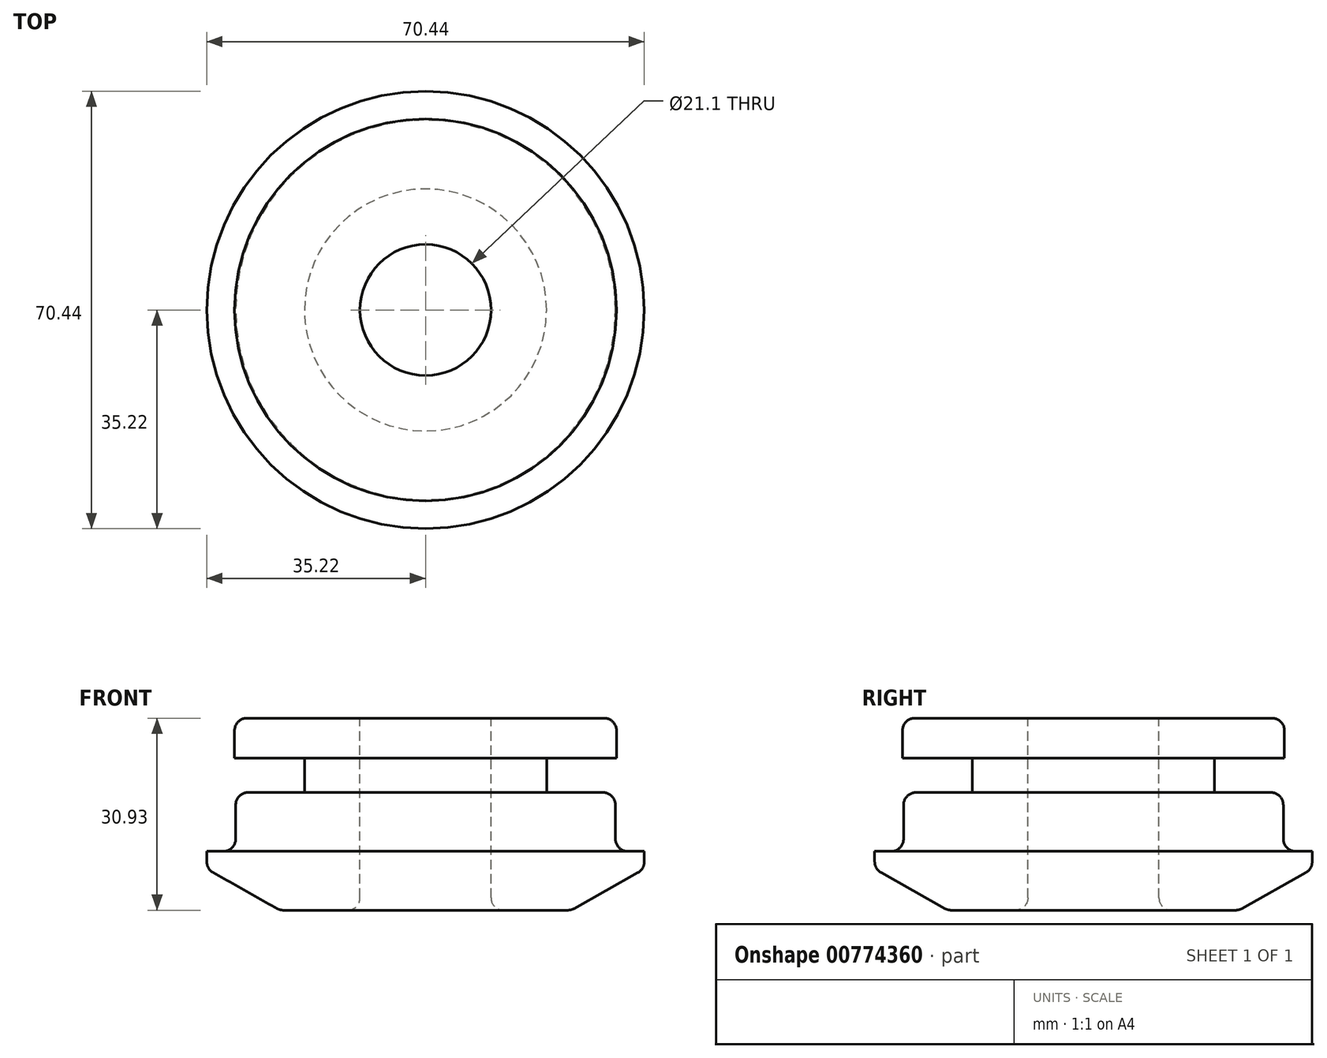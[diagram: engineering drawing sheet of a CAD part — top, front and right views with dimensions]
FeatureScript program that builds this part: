
annotation { "Feature Type Name" : "Feature", "Feature Type Description" : "" }
export const myFeature = defineFeature(function(context is Context, id is Id, definition is map)
    precondition{}
    {
        {
            var Q0;
            Q0=qCreatedBy(makeId("Front.planeOp"),FACE);
            var sketch = newSketch(context, id + "F0", { "sketchPlane" : qUnion([Q0])});
            skLineSegment(sketch, "E0", {"start": v(0, 55.06) * mm, "end": v(0, -43.98) * mm});
            skLineSegment(sketch, "E1", {"start": v(10.55, 5.54) * mm, "end": v(10.55, 36.47) * mm});
            skPoint(sketch, "E1.startSnap0", {"position": v(0, 5.54) * mm});
            skLineSegment(sketch, "E2", {"start": v(10.55, 36.47) * mm, "end": v(30.75, 36.47) * mm});
            skLineSegment(sketch, "E3", {"start": v(30.75, 36.47) * mm, "end": v(30.75, 30.03) * mm});
            skLineSegment(sketch, "E4", {"start": v(30.75, 30.03) * mm, "end": v(19.49, 30.03) * mm});
            skLineSegment(sketch, "E5", {"start": v(19.49, 30.03) * mm, "end": v(19.49, 24.5) * mm});
            skLineSegment(sketch, "E6", {"start": v(19.49, 24.5) * mm, "end": v(30.57, 24.5) * mm});
            skLineSegment(sketch, "E7", {"start": v(30.57, 24.5) * mm, "end": v(30.57, 15.02) * mm});
            skLineSegment(sketch, "E8", {"start": v(30.57, 15.02) * mm, "end": v(35.22, 15.02) * mm});
            skLineSegment(sketch, "E9", {"start": v(35.22, 15.02) * mm, "end": v(35.22, 12.16) * mm});
            skLineSegment(sketch, "E10", {"start": v(35.22, 12.16) * mm, "end": v(23.42, 5.54) * mm});
            skLineSegment(sketch, "E11", {"start": v(23.42, 5.54) * mm, "end": v(10.55, 5.54) * mm});
            skSolve(sketch);
        }
        {
            var Q0;
            Q0 = qSketchRegion(id + "F0", true);
            var Q1;
            Q1=sQuery(id+"F0.wireOp",EDGE,"E0");
            revolve(context, id + "F1", {"surfaceOperationType" : NewSurfaceOperationType.NEW, "entities" : qUnion([Q0]), "axis" : qUnion([Q1]), "revolveType" : RevolveType.FULL});
        }
        {
            var Q0;
            Q0=makeQuery(id+"F1.opRevolve","SWEPT_EDGE",EDGE,{"disambiguationData":[OSD([sQuery(id+"F0.wireOp",EDGE,"E2"),sQuery(id+"F0.wireOp",EDGE,"E3")])]});
            var Q1;
            Q1=makeQuery(id+"F1.opRevolve","SWEPT_FACE",FACE,{"disambiguationData":[OSD([sQuery(id+"F0.wireOp",EDGE,"E7")])]});
            fillet(context, id + "F2", {"entities" : qUnion([Q0, Q1]), "radius" : 2 * mm, "tangentPropagation" : true, "allowEdgeOverflow" : false});
        }
        {
            var Q0;
            Q0=makeQuery(id+"F1.opRevolve","SWEPT_EDGE",EDGE,{"disambiguationData":[OSD([sQuery(id+"F0.wireOp",EDGE,"E9"),sQuery(id+"F0.wireOp",EDGE,"E10")])]});
            var Q1;
            Q1=makeQuery(id+"F1.opRevolve","SWEPT_EDGE",EDGE,{"disambiguationData":[OSD([sQuery(id+"F0.wireOp",EDGE,"E10"),sQuery(id+"F0.wireOp",EDGE,"E11")])]});
            var Q2;
            Q2=makeQuery(id+"F1.opRevolve","SWEPT_EDGE",EDGE,{"disambiguationData":[OSD([sQuery(id+"F0.wireOp",EDGE,"E1"),sQuery(id+"F0.wireOp",EDGE,"E11")])]});
            fillet(context, id + "F3", {"entities" : qUnion([Q0, Q1, Q2]), "radius" : 2 * mm, "tangentPropagation" : true, "allowEdgeOverflow" : false});
        }
    });
